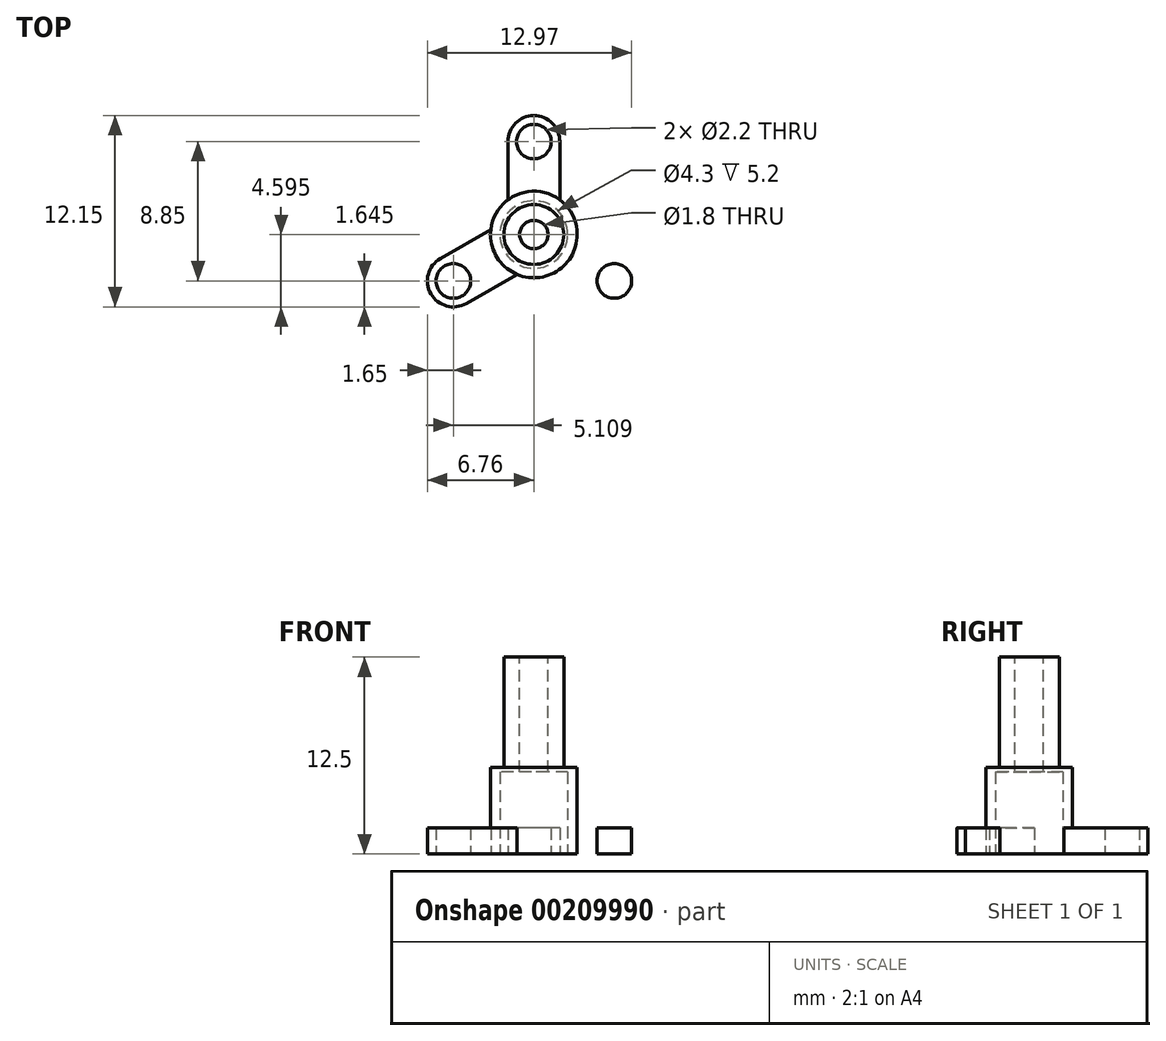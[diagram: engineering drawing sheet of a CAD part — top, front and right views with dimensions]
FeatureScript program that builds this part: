
annotation { "Feature Type Name" : "Feature", "Feature Type Description" : "" }
export const myFeature = defineFeature(function(context is Context, id is Id, definition is map)
    precondition{}
    {
        {
            var Q0;
            Q0=qCreatedBy(makeId("Top.planeOp"),FACE);
            var sketch = newSketch(context, id + "F0", { "sketchPlane" : qUnion([Q0])});
            skCircle(sketch, "E0", {"center": v(-11.04, 11.55) * mm, "radius": 2.75 * mm});
            skCircle(sketch, "E1", {"center": v(-11.04, 11.55) * mm, "radius": 2.15 * mm});
            skLineSegment(sketch, "E2", {"start": v(-11.04, 11.55) * mm, "end": v(-11.04, 23.86) * mm, "construction": true});
            skLineSegment(sketch, "E3", {"start": v(-11.04, 23.86) * mm, "end": v(-11.04, 11.55) * mm, "construction": true});
            skLineSegment(sketch, "E4", {"start": v(-11.04, 11.55) * mm, "end": v(3.9, 2.92) * mm, "construction": true});
            skLineSegment(sketch, "E5", {"start": v(-11.04, 11.55) * mm, "end": v(-25.98, 2.92) * mm, "construction": true});
            skCircle(sketch, "E6", {"center": v(-11.04, 13.7) * mm, "radius": 3 * mm, "construction": true});
            skLineSegment(sketch, "E7", {"start": v(-11.04, 16.7) * mm, "end": v(-6.47, 16.7) * mm, "construction": true});
            skLineSegment(sketch, "E8", {"start": v(-7.49, 16.7) * mm, "end": v(-7.49, 17.45) * mm, "construction": true});
            skLineSegment(sketch, "E9", {"start": v(-11.04, 11.55) * mm, "end": v(2.67, 19.46) * mm, "construction": true});
            skLineSegment(sketch, "E10", {"start": v(-9.04, 13.43) * mm, "end": v(-9.04, 13.43) * mm});
            skLineSegment(sketch, "E11", {"start": v(-11.04, 14.3) * mm, "end": v(-6.28, 14.3) * mm, "construction": true});
            skLineSegment(sketch, "E12", {"start": v(-11.04, 13.7) * mm, "end": v(-0.7, 13.43) * mm, "construction": true});
            skLineSegment(sketch, "E13", {"start": v(-7.49, 17.45) * mm, "end": v(-16.51, 17.45) * mm, "construction": true});
            skCircle(sketch, "E14", {"center": v(-11.04, 17.45) * mm, "radius": 1.1 * mm});
            skPoint(sketch, "E15.orphan", {"position": v(-13.04, 18.35) * mm});
            skPoint(sketch, "E16.orphan", {"position": v(-9.04, 18.35) * mm});
            skCircle(sketch, "E17", {"center": v(-11.04, 17.45) * mm, "radius": 1.65 * mm, "construction": true});
            skLineSegment(sketch, "E18", {"start": v(-12.7, 17.45) * mm, "end": v(-12.7, 13.75) * mm});
            skArc(sketch, "E19", {"start": v(-9.4, 17.45) * mm, "mid": v(-11.04, 19.1) * mm, "end": v(-12.7, 17.45) * mm});
            skLineSegment(sketch, "E20", {"start": v(-9.4, 17.45) * mm, "end": v(-9.4, 13.75) * mm});
            skCircle(sketch, "E21.MirrorC", {"center": v(-5.93, 8.6) * mm, "radius": 1.1 * mm});
            skLineSegment(sketch, "E22.MirrorCS", {"start": v(-6.76, 7.17) * mm, "end": v(-9.96, 9.02) * mm});
            skLineSegment(sketch, "E23.MirrorCS", {"start": v(-5.1, 10.02) * mm, "end": v(-8.3, 11.87) * mm});
            skArc(sketch, "E24", {"start": v(-6.76, 7.17) * mm, "mid": v(-4.5, 7.77) * mm, "end": v(-5.1, 10.02) * mm});
            skLineSegment(sketch, "E25.MirrorCS", {"start": v(-16.97, 10.02) * mm, "end": v(-13.77, 11.87) * mm});
            skArc(sketch, "E26.MirrorCS", {"start": v(-15.32, 7.17) * mm, "mid": v(-17.58, 7.77) * mm, "end": v(-16.97, 10.02) * mm});
            skCircle(sketch, "E27.MirrorC", {"center": v(-16.15, 8.6) * mm, "radius": 1.1 * mm});
            skLineSegment(sketch, "E28.MirrorCS", {"start": v(-15.32, 7.17) * mm, "end": v(-12.12, 9.02) * mm});
            skSolve(sketch);
        }
        {
            var Q0;
            Q0=makeQuery(id+"F0.imprint","IMPRINT",FACE,{"disambiguationData":[TD([[makeQuery(id+"F0.imprint","IMPRINT",EDGE,{"derivedFrom":sQuery(id+"F0.wireOp",EDGE,"E14")}),-1.0]])]});
            var Q1;
            Q1=makeQuery(id+"F0.imprint","IMPRINT",FACE,{"disambiguationData":[TD([[makeQuery(id+"F0.imprint","IMPRINT",EDGE,{"derivedFrom":sQuery(id+"F0.wireOp",EDGE,"E1")}),-1.0]])]});
            var Q2;
            Q2=makeQuery(id+"F0.imprint","IMPRINT",FACE,{"disambiguationData":[TD([[makeQuery(id+"F0.imprint","IMPRINT",EDGE,{"derivedFrom":sQuery(id+"F0.wireOp",EDGE,"E21.MirrorC")}),1.0]])]});
            var Q3;
            {var subQ0=sQuery(id+"F0.wireOp",EDGE,"E25.MirrorCS");Q3=makeQuery(id+"F0.imprint","IMPRINT",FACE,{"disambiguationData":[TD([[makeQuery(id+"F0.imprint","IMPRINT",EDGE,{"derivedFrom":subQ0}),-1.0]])]});}
            extrude(context, id + "F1", {"entities" : qUnion([Q0, Q1, Q2, Q3]), "depth" : 1.65 * mm});
        }
        {
            var Q0;
            Q0=makeQuery(id+"F1.opExtrude","CAP_FACE",FACE,{"disambiguationData":[OSD([sQuery(id+"F0.wireOp",EDGE,"E0"),sQuery(id+"F0.wireOp",EDGE,"E1"),sQuery(id+"F0.wireOp",EDGE,"fwkbj9af-bvW2-zXIo-DP0X-yjGYd7fJuAXA"),sQuery(id+"F0.wireOp",EDGE,"527f2c15-93a8-4ae9-ba0b-32c85fabb12b0.MirrorCS"),sQuery(id+"F0.wireOp",EDGE,"E14"),sQuery(id+"F0.wireOp",EDGE,"eQcchlES-lFoi-6n4S-Yad0-nxIxKA4x8ylb"),sQuery(id+"F0.wireOp",EDGE,"ca3c6fec-599a-4702-8f71-3eb269a536c50.MirrorCS"),sQuery(id+"F0.wireOp",EDGE,"91d6acf3-96d5-40d6-8d8c-d6aea248ae770.MirrorC"),sQuery(id+"F0.wireOp",EDGE,"6f703371-d952-44e0-a788-3b89ca1275450.MirrorCS"),sQuery(id+"F0.wireOp",EDGE,"bec68641-e7b0-4ac3-9c77-0c98deaedfe60.MirrorCS"),sQuery(id+"F0.wireOp",EDGE,"e6cfb6a1-a5a3-4a68-b189-c31deaa66c9d0.MirrorCS"),sQuery(id+"F0.wireOp",EDGE,"d4d0f112-965c-4a49-a081-eb552d3093480.MirrorC"),sQuery(id+"F0.wireOp",EDGE,"5edd3b1d-4707-4fb8-be1a-2457a2320f160.MirrorCS"),sQuery(id+"F0.wireOp",EDGE,"df4d6a8f-55ab-4714-90df-786a673838060.MirrorCS")])],"isStart":false});
            var sketch = newSketch(context, id + "F2", { "sketchPlane" : qUnion([Q0])});
            skPoint(sketch, "E29.first.point", {"position": v(-12.7, 13.75) * mm});
            skPoint(sketch, "E29.second.point", {"position": v(-12.7, 13.75) * mm});
            skPoint(sketch, "E29.third.point", {"position": v(-12.7, 13.75) * mm});
            skCircle(sketch, "E30", {"center": v(-11.04, 11.55) * mm, "radius": 2.15 * mm});
            skPoint(sketch, "E30.first.point", {"position": v(-11.02, 13.7) * mm});
            skPoint(sketch, "E30.second.point", {"position": v(-12.87, 10.41) * mm});
            skPoint(sketch, "E30.third.point", {"position": v(-9.17, 10.49) * mm});
            skCircle(sketch, "E31", {"center": v(-11.04, 11.55) * mm, "radius": 2.75 * mm});
            skSolve(sketch);
        }
        {
            var Q0;
            Q0=makeQuery(id+"F2.imprint","IMPRINT",FACE,{"disambiguationData":[TD([[makeQuery(id+"F2.imprint","IMPRINT",EDGE,{"derivedFrom":sQuery(id+"F2.wireOp",EDGE,"E30")}),-1.0]])]});
            extrude(context, id + "F3", {"entities" : qUnion([Q0]), "operationType" : NewBodyOperationType.ADD, "depth" : 3.85 * mm});
        }
        {
            var Q0;
            Q0=makeQuery(id+"F3.opExtrude","CAP_FACE",FACE,{"disambiguationData":[OSD([sQuery(id+"F2.wireOp",EDGE,"b10bdf0c-fa09-4bd3-9bf7-7f028818a10e"),sQuery(id+"F2.wireOp",EDGE,"E30")])],"isStart":false});
            var sketch = newSketch(context, id + "F4", { "sketchPlane" : qUnion([Q0])});
            skCircle(sketch, "E32", {"center": v(-11.04, 11.55) * mm, "radius": 2.15 * mm});
            skPoint(sketch, "E32.first.point", {"position": v(-12.04, 13.45) * mm});
            skPoint(sketch, "E32.second.point", {"position": v(-12.57, 10.04) * mm});
            skPoint(sketch, "E32.third.point", {"position": v(-9.01, 10.83) * mm});
            skCircle(sketch, "E33", {"center": v(-11.04, 11.55) * mm, "radius": 1.9 * mm});
            skCircle(sketch, "E34", {"center": v(-11.04, 11.55) * mm, "radius": 0.9 * mm});
            skSolve(sketch);
        }
        {
            var Q0;
            Q0=makeQuery(id+"F4.imprint","IMPRINT",FACE,{"disambiguationData":[TD([[makeQuery(id+"F4.imprint","IMPRINT",EDGE,{"derivedFrom":sQuery(id+"F4.wireOp",EDGE,"E32")}),1.0]])]});
            var Q1;
            Q1=makeQuery(id+"F4.imprint","IMPRINT",FACE,{"disambiguationData":[TD([[makeQuery(id+"F4.imprint","IMPRINT",EDGE,{"derivedFrom":sQuery(id+"F4.wireOp",EDGE,"E33")}),1.0]])]});
            extrude(context, id + "F5", {"entities" : qUnion([Q0, Q1]), "operationType" : NewBodyOperationType.ADD, "oppositeDirection" : true, "depth" : 0.3 * mm});
        }
        {
            var Q0;
            Q0=makeQuery(id+"F4.imprint","IMPRINT",FACE,{"disambiguationData":[TD([[makeQuery(id+"F4.imprint","IMPRINT",EDGE,{"derivedFrom":sQuery(id+"F4.wireOp",EDGE,"E33")}),1.0]])]});
            extrude(context, id + "F6", {"entities" : qUnion([Q0]), "operationType" : NewBodyOperationType.ADD, "depth" : 7 * mm});
        }
    });
